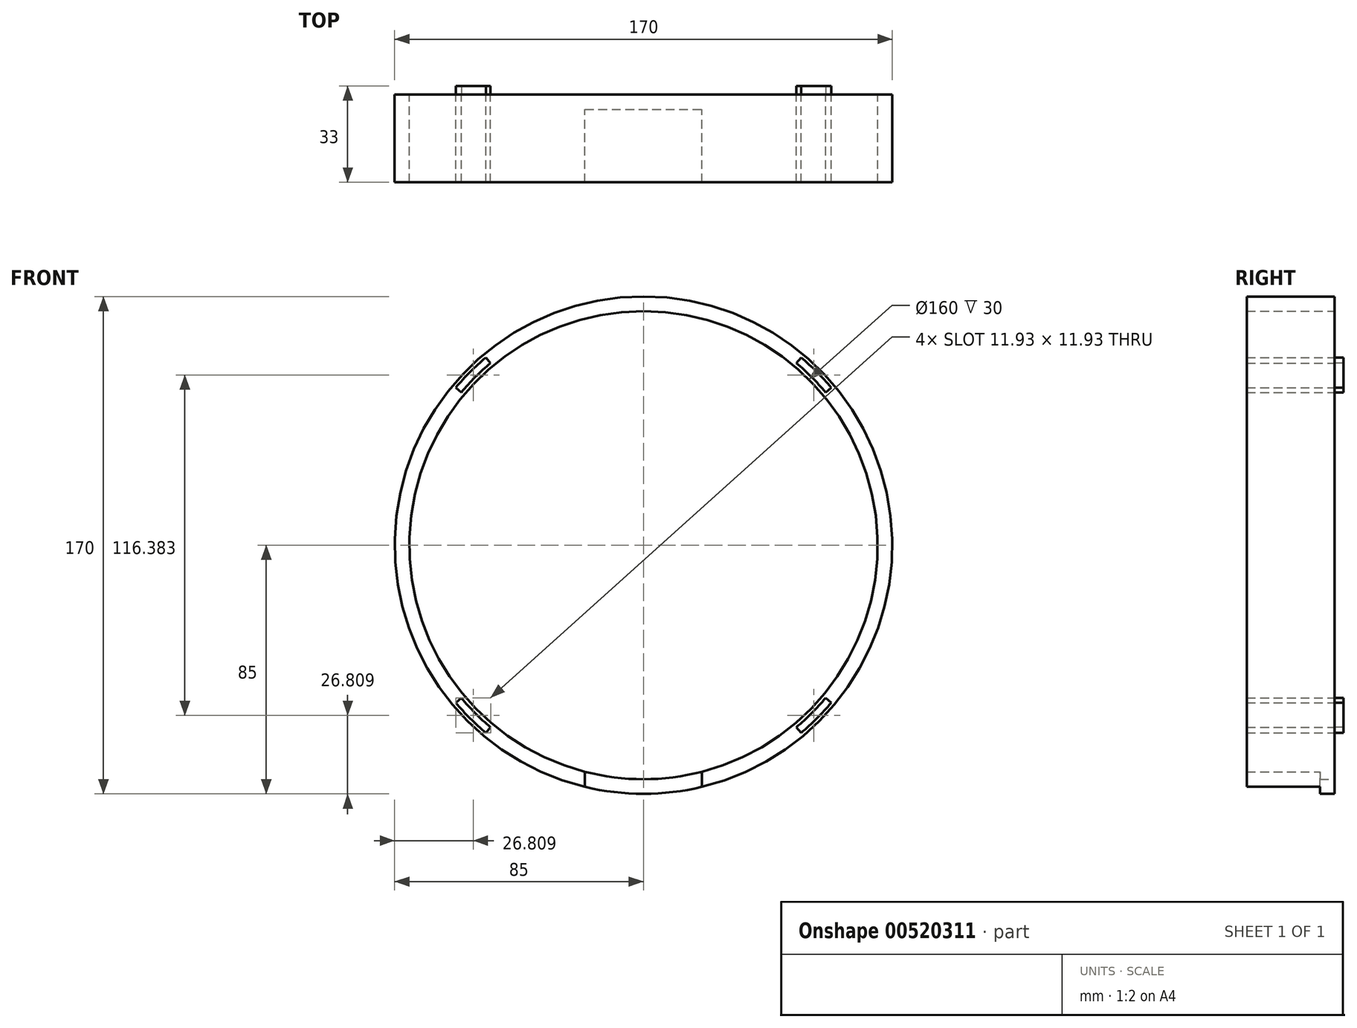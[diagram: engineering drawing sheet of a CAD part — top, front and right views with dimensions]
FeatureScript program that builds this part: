
annotation { "Feature Type Name" : "Feature", "Feature Type Description" : "" }
export const myFeature = defineFeature(function(context is Context, id is Id, definition is map)
    precondition{}
    {
        {
            var Q0;
            Q0=qCreatedBy(makeId("Front.planeOp"),FACE);
            var sketch = newSketch(context, id + "F0", { "sketchPlane" : qUnion([Q0])});
            skCircle(sketch, "E0", {"center": v(0, 0) * mm, "radius": 80 * mm});
            skCircle(sketch, "E1", {"center": v(0, 0) * mm, "radius": 85 * mm});
            skLineSegment(sketch, "E2", {"start": v(52.23, -62.24) * mm, "end": v(53.83, -64.16) * mm});
            skLineSegment(sketch, "E3", {"start": v(64.16, -53.83) * mm, "end": v(62.24, -52.23) * mm});
            skArc(sketch, "E4", {"start": v(52.23, -62.24) * mm, "mid": v(57.45, -57.45) * mm, "end": v(62.24, -52.23) * mm});
            skArc(sketch, "E5", {"start": v(53.83, -64.16) * mm, "mid": v(59.22, -59.22) * mm, "end": v(64.16, -53.83) * mm});
            skLineSegment(sketch, "E6", {"start": v(-64.16, -53.83) * mm, "end": v(-62.24, -52.23) * mm});
            skLineSegment(sketch, "E7", {"start": v(-53.83, -64.16) * mm, "end": v(-52.23, -62.24) * mm});
            skArc(sketch, "E8", {"start": v(-62.24, -52.23) * mm, "mid": v(-57.45, -57.45) * mm, "end": v(-52.23, -62.24) * mm});
            skArc(sketch, "E9", {"start": v(-64.16, -53.83) * mm, "mid": v(-59.22, -59.22) * mm, "end": v(-53.83, -64.16) * mm});
            skLineSegment(sketch, "E10", {"start": v(-53.83, 64.16) * mm, "end": v(-52.23, 62.24) * mm});
            skLineSegment(sketch, "E11", {"start": v(-64.16, 53.83) * mm, "end": v(-62.24, 52.23) * mm});
            skArc(sketch, "E12", {"start": v(-62.24, 52.23) * mm, "mid": v(-57.45, 57.45) * mm, "end": v(-52.23, 62.24) * mm});
            skArc(sketch, "E13", {"start": v(-64.16, 53.83) * mm, "mid": v(-59.22, 59.22) * mm, "end": v(-53.83, 64.16) * mm});
            skLineSegment(sketch, "E14", {"start": v(64.16, 53.83) * mm, "end": v(62.24, 52.23) * mm});
            skLineSegment(sketch, "E15", {"start": v(53.83, 64.16) * mm, "end": v(52.23, 62.24) * mm});
            skArc(sketch, "E16", {"start": v(52.23, 62.24) * mm, "mid": v(57.45, 57.45) * mm, "end": v(62.24, 52.23) * mm});
            skArc(sketch, "E17", {"start": v(64.16, 53.83) * mm, "mid": v(59.22, 59.22) * mm, "end": v(53.83, 64.16) * mm});
            skLineSegment(sketch, "E18", {"start": v(0, 0) * mm, "end": v(-20, 0) * mm, "construction": true});
            skLineSegment(sketch, "E19", {"start": v(0, 0) * mm, "end": v(20, 0) * mm, "construction": true});
            skLineSegment(sketch, "E20", {"start": v(-20, -75.8) * mm, "end": v(-20, -87.84) * mm});
            skLineSegment(sketch, "E21", {"start": v(20, -87.84) * mm, "end": v(20, -75.8) * mm});
            skSolve(sketch);
        }
        {
            var Q0;
            Q0=qSketchRegion(id+"F0",true);
            extrude(context, id + "F1", {"entities" : qUnion([Q0]), "depth" : 30 * mm, "offsetDistance" : 25 * mm});
        }
        {
            var Q0;
            Q0=makeQuery(id+"F0.imprint","IMPRINT",FACE,{"disambiguationData":[TD([[makeQuery(id+"F0.imprint","IMPRINT",EDGE,{"derivedFrom":sQuery(id+"F0.wireOp",EDGE,"E10")}),-1.0]])]});
            var Q1;
            Q1=makeQuery(id+"F0.imprint","IMPRINT",FACE,{"disambiguationData":[TD([[makeQuery(id+"F0.imprint","IMPRINT",EDGE,{"derivedFrom":sQuery(id+"F0.wireOp",EDGE,"E14")}),-1.0]])]});
            var Q2;
            Q2=makeQuery(id+"F0.imprint","IMPRINT",FACE,{"disambiguationData":[TD([[makeQuery(id+"F0.imprint","IMPRINT",EDGE,{"derivedFrom":sQuery(id+"F0.wireOp",EDGE,"E2")}),1.0]])]});
            var Q3;
            Q3=makeQuery(id+"F0.imprint","IMPRINT",FACE,{"disambiguationData":[TD([[makeQuery(id+"F0.imprint","IMPRINT",EDGE,{"derivedFrom":sQuery(id+"F0.wireOp",EDGE,"E6")}),-1.0]])]});
            extrude(context, id + "F2", {"entities" : qUnion([Q0, Q1, Q2, Q3]), "oppositeDirection" : true, "depth" : 3 * mm, "offsetDistance" : 25 * mm});
        }
        {
            var Q0;
            Q0=makeQuery(id+"F0.imprint","IMPRINT",FACE,{"disambiguationData":[TD([[makeQuery(id+"F0.imprint","IMPRINT",EDGE,{"derivedFrom":sQuery(id+"F0.wireOp",EDGE,"E10")}),-1.0]])]});
            var Q1;
            Q1=makeQuery(id+"F0.imprint","IMPRINT",FACE,{"disambiguationData":[TD([[makeQuery(id+"F0.imprint","IMPRINT",EDGE,{"derivedFrom":sQuery(id+"F0.wireOp",EDGE,"E6")}),-1.0]])]});
            var Q2;
            Q2=makeQuery(id+"F0.imprint","IMPRINT",FACE,{"disambiguationData":[TD([[makeQuery(id+"F0.imprint","IMPRINT",EDGE,{"derivedFrom":sQuery(id+"F0.wireOp",EDGE,"E2")}),1.0]])]});
            var Q3;
            Q3=makeQuery(id+"F0.imprint","IMPRINT",FACE,{"disambiguationData":[TD([[makeQuery(id+"F0.imprint","IMPRINT",EDGE,{"derivedFrom":sQuery(id+"F0.wireOp",EDGE,"E14")}),-1.0]])]});
            extrude(context, id + "F3", {"entities" : qUnion([Q0, Q1, Q2, Q3]), "depth" : 30 * mm, "offsetDistance" : 25 * mm});
        }
        {
            var Q0;
            {var subQ0=sQuery(id+"F0.wireOp",EDGE,"E20");var subQ1=sQuery(id+"F0.wireOp",EDGE,"E0");var subQ2=makeQuery(id+"F0.imprint","INTERSECT",VERTEX,{"derivedFrom":[subQ1,subQ0]});Q0=makeQuery(id+"F0.imprint","IMPRINT",FACE,{"disambiguationData":[TD([[makeQuery(id+"F0.imprint","IMPRINT",EDGE,{"disambiguationData":[TD([[subQ2,-1.0]])],"derivedFrom":subQ1}),-1.0]])]});}
            extrude(context, id + "F4", {"entities" : qUnion([Q0]), "operationType" : NewBodyOperationType.REMOVE, "depth" : 30 * mm, "offsetDistance" : 25 * mm});
        }
        {
            var Q0;
            {var subQ0=sQuery(id+"F0.wireOp",EDGE,"E20");var subQ1=sQuery(id+"F0.wireOp",EDGE,"E0");var subQ2=makeQuery(id+"F0.imprint","INTERSECT",VERTEX,{"derivedFrom":[subQ1,subQ0]});Q0=makeQuery(id+"F0.imprint","IMPRINT",FACE,{"disambiguationData":[TD([[makeQuery(id+"F0.imprint","IMPRINT",EDGE,{"disambiguationData":[TD([[subQ2,-1.0]])],"derivedFrom":subQ1}),-1.0]])]});}
            extrude(context, id + "F5", {"entities" : qUnion([Q0]), "operationType" : NewBodyOperationType.ADD, "depth" : 5 * mm, "offsetDistance" : 25 * mm});
        }
    });
